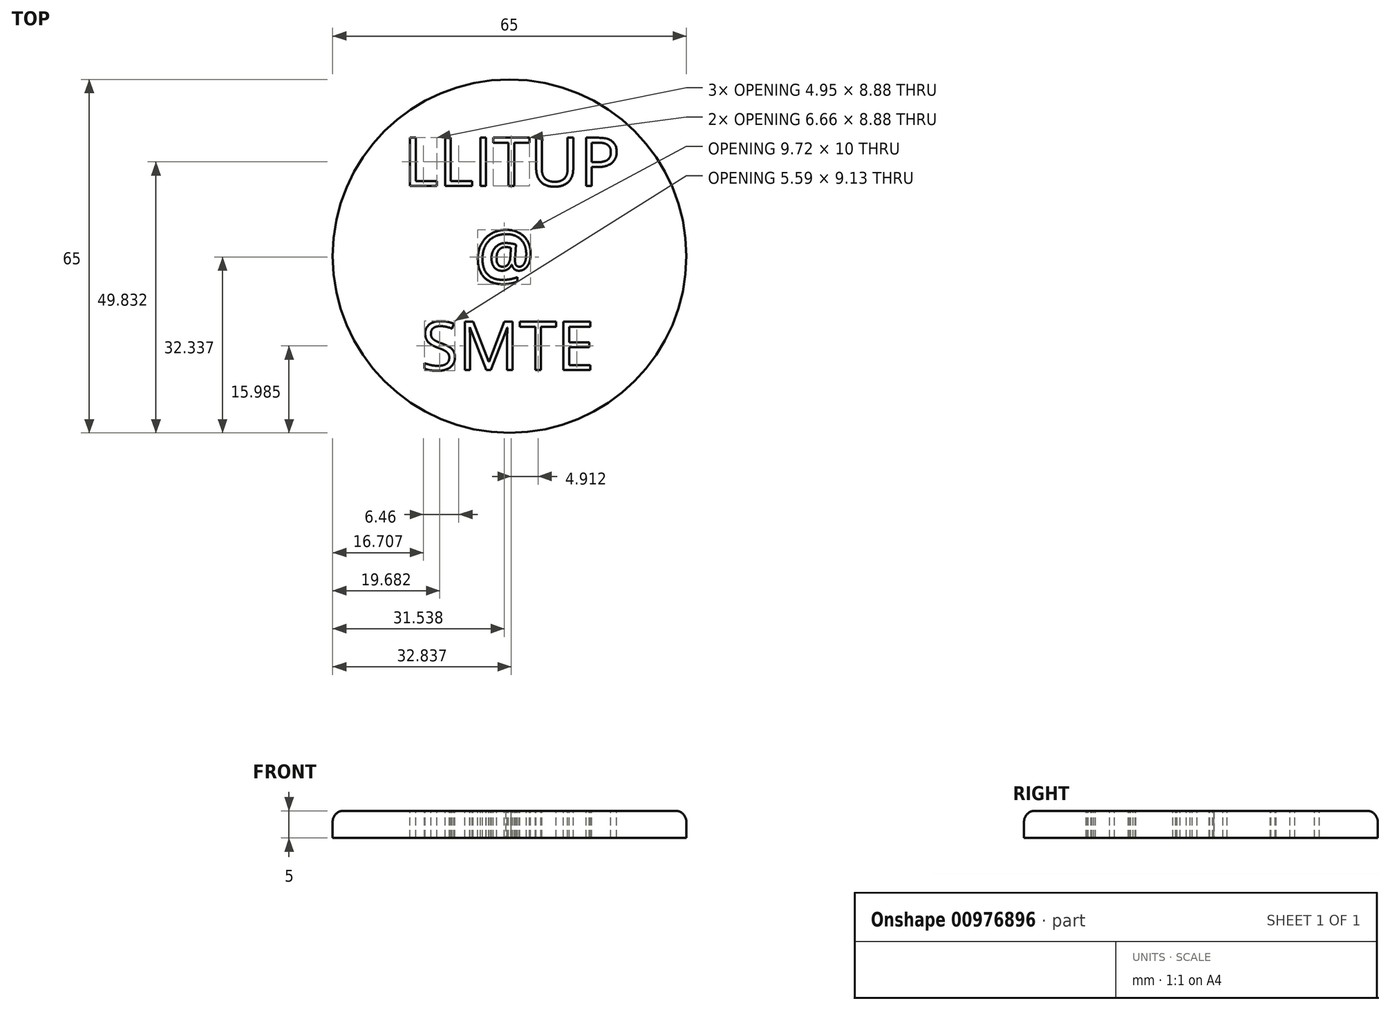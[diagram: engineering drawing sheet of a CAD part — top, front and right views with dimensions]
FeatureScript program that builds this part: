
annotation { "Feature Type Name" : "Feature", "Feature Type Description" : "" }
export const myFeature = defineFeature(function(context is Context, id is Id, definition is map)
    precondition{}
    {
        {
            var Q0;
            Q0=qCreatedBy(makeId("Top.planeOp"),FACE);
            var sketch = newSketch(context, id + "F0", { "sketchPlane" : qUnion([Q0])});
            skCircle(sketch, "E0", {"center": v(0, 0) * mm, "radius": 32.5 * mm});
            skSolve(sketch);
        }
        {
            var Q0;
            Q0 = qSketchRegion(id + "F0", true);
            extrude(context, id + "F1", {"entities" : qUnion([Q0]), "depth" : 5 * mm, "offsetDistance" : 25 * mm});
        }
        {
            var Q0;
            Q0=makeQuery(id+"F1.opExtrude","CAP_FACE",FACE,{"disambiguationData":[OSD([sQuery(id+"F0.wireOp",EDGE,"E0")])],"isStart":false});
            var sketch = newSketch(context, id + "F2", { "sketchPlane" : qUnion([Q0])});
            skText(sketch, "E1", { "text": "LLITUP\n    @\n SMTE", "fontName": "OpenSans-Regular.ttf"});
            const initialGuessF2  = {"E1": [-0.01949, 0.01289, 1, 0, 0.00896]};
            skSetInitialGuess(sketch, initialGuessF2);
            skSolve(sketch);
        }
        {
            var Q0;
            Q0 = qSketchRegion(id + "F2", true);
            extrude(context, id + "F3", {"entities" : qUnion([Q0]), "operationType" : NewBodyOperationType.REMOVE, "endBound" : BoundingType.THROUGH_ALL, "oppositeDirection" : true, "depth" : 25 * mm, "offsetDistance" : 25 * mm});
        }
        {
            var Q0;
            Q0=makeQuery(id+"F1.opExtrude","CAP_EDGE",EDGE,{"disambiguationData":[OSD([sQuery(id+"F0.wireOp",EDGE,"E0")])],"isStart":false});
            fillet(context, id + "F4", {"entities" : qUnion([Q0]), "radius" : 2 * mm, "tangentPropagation" : true, "allowEdgeOverflow" : false});
        }
    });
